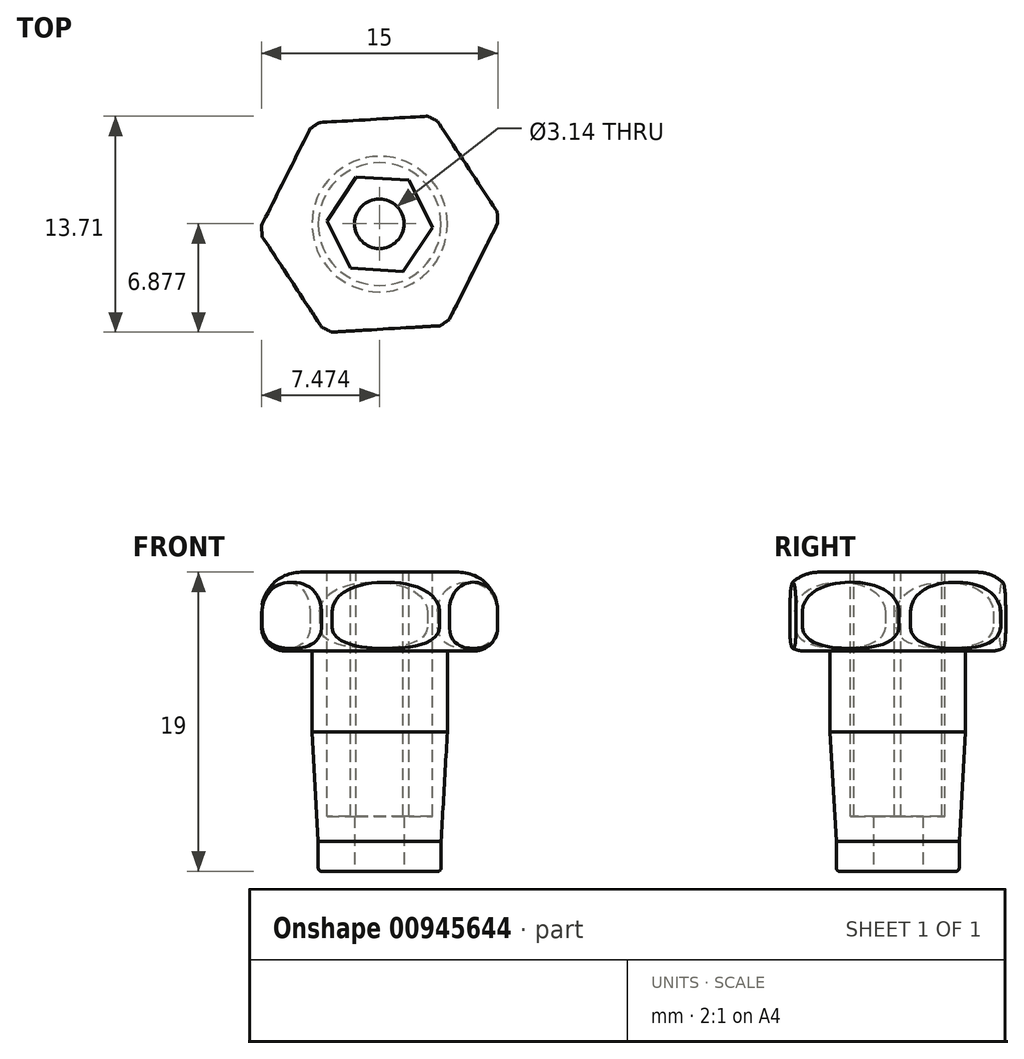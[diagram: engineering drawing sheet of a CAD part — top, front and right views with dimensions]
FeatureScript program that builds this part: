
annotation { "Feature Type Name" : "Feature", "Feature Type Description" : "" }
export const myFeature = defineFeature(function(context is Context, id is Id, definition is map)
    precondition{}
    {
        {
            var Q0;
            Q0=qCreatedBy(makeId("Top.planeOp"),FACE);
            var sketch = newSketch(context, id + "F0", { "sketchPlane" : qUnion([Q0])});
            skCircle(sketch, "E0", {"center": v(-41.47, -26.1) * mm, "radius": 3.9 * mm});
            skSolve(sketch);
        }
        {
            var Q0;
            Q0=qCreatedBy(makeId("Top.planeOp"),FACE);
            var sketch = newSketch(context, id + "F1", { "sketchPlane" : qUnion([Q0])});
            skCircle(sketch, "E1", {"center": v(-41.5, -26.07) * mm, "radius": 1.57 * mm});
            skSolve(sketch);
        }
        {
            var Q0;
            Q0=qSketchRegion(id+"F0",true);
            extrude(context, id + "F2", {"entities" : qUnion([Q0]), "depth" : 14 * mm, "offsetDistance" : 25 * mm});
        }
        {
            var Q0;
            Q0=makeQuery(id+"F2.opExtrude","CAP_FACE",FACE,{"disambiguationData":[OSD([sQuery(id+"F0.wireOp",EDGE,"E0")])],"isStart":false});
            var sketch = newSketch(context, id + "F3", { "sketchPlane" : qUnion([Q0])});
            skCircle(sketch, "E2", {"center": v(-41.47, -26.1) * mm, "radius": 7.5 * mm});
            skSolve(sketch);
        }
        {
            var Q0;
            Q0=qSketchRegion(id+"F3",true);
            extrude(context, id + "F4", {"entities" : qUnion([Q0]), "operationType" : NewBodyOperationType.ADD, "depth" : 5 * mm, "offsetDistance" : 25 * mm});
        }
        {
            var Q0;
            Q0=makeQuery(id+"F4.opExtrude","CAP_FACE",FACE,{"disambiguationData":[OSD([sQuery(id+"F3.wireOp",EDGE,"E2")])],"isStart":false});
            var sketch = newSketch(context, id + "F5", { "sketchPlane" : qUnion([Q0])});
            skCircle(sketch, "E3.cCircle", {"center": v(-41.47, -26.1) * mm, "radius": 2.9 * mm, "construction": true});
            skLineSegment(sketch, "E3.0", {"start": v(-38.13, -26.3) * mm, "end": v(-39.98, -29.1) * mm});
            skLineSegment(sketch, "E3.1", {"start": v(-39.98, -29.1) * mm, "end": v(-43.32, -28.89) * mm});
            skLineSegment(sketch, "E3.2", {"start": v(-43.32, -28.89) * mm, "end": v(-44.81, -25.89) * mm});
            skLineSegment(sketch, "E3.3", {"start": v(-44.81, -25.89) * mm, "end": v(-42.97, -23.1) * mm});
            skLineSegment(sketch, "E3.4", {"start": v(-42.97, -23.1) * mm, "end": v(-39.62, -23.3) * mm});
            skLineSegment(sketch, "E3.5", {"start": v(-39.62, -23.3) * mm, "end": v(-38.13, -26.3) * mm});
            skPoint(sketch, "E3.0.midPoint", {"position": v(-39.05, -27.7) * mm});
            skSolve(sketch);
        }
        {
            var Q0;
            {var subQ0=sQuery(id+"F3.wireOp",EDGE,"E2");Q0=makeQuery(id+"F4.boolean.opBoolean","SPLIT",FACE,{"disambiguationData":[TD([makeQuery(id+"F2.opExtrude","SWEPT_FACE",FACE,{"disambiguationData":[OSD([sQuery(id+"F0.wireOp",EDGE,"E0")])]})])],"derivedFrom":makeQuery(id+"F4.opExtrude","CAP_FACE",FACE,{"disambiguationData":[OSD([subQ0])],"isStart":true})});}
            var sketch = newSketch(context, id + "F6", { "sketchPlane" : qUnion([Q0])});
            skCircle(sketch, "E4", {"center": v(-41.47, 26.1) * mm, "radius": 4.3 * mm});
            skSolve(sketch);
        }
        {
            var Q0;
            Q0=qSketchRegion(id+"F6",true);
            extrude(context, id + "F7", {"entities" : qUnion([Q0]), "operationType" : NewBodyOperationType.ADD, "depth" : 4.1 * mm, "offsetDistance" : 25 * mm});
        }
        {
            var Q0;
            Q0=qSketchRegion(id+"F1",true);
            extrude(context, id + "F8", {"entities" : qUnion([Q0]), "operationType" : NewBodyOperationType.REMOVE, "depth" : 23.4 * mm, "offsetDistance" : 25 * mm});
        }
        {
            var Q0;
            Q0=qSketchRegion(id+"F5",true);
            extrude(context, id + "F9", {"entities" : qUnion([Q0]), "operationType" : NewBodyOperationType.REMOVE, "oppositeDirection" : true, "depth" : 15.5 * mm, "offsetDistance" : 25 * mm});
        }
        {
            var Q0;
            Q0=makeQuery(id+"F2.opExtrude","CAP_EDGE",EDGE,{"disambiguationData":[OSD([sQuery(id+"F0.wireOp",EDGE,"E0")])],"isStart":true});
            fillet(context, id + "F10", {"entities" : qUnion([Q0]), "radius" : 0.2 * mm, "tangentPropagation" : true, "allowEdgeOverflow" : false});
        }
        {
            var Q0;
            Q0=makeQuery(id+"F7.boolean.opBoolean","INTERSECT",EDGE,{"derivedFrom":[makeQuery(id+"F2.opExtrude","SWEPT_FACE",FACE,{"disambiguationData":[OSD([sQuery(id+"F0.wireOp",EDGE,"E0")])]}),makeQuery(id+"F7.opExtrude","CAP_FACE",FACE,{"disambiguationData":[OSD([sQuery(id+"F6.wireOp",EDGE,"E4")])],"isStart":false})]});
            chamfer(context, id + "F11", {"entities" : qUnion([Q0]), "chamferType" : ChamferType.OFFSET_ANGLE, "width" : 8 * mm, "oppositeDirection" : false, "angle" : 3.3 * degree, "tangentPropagation" : true});
        }
        {
            var Q0;
            Q0=makeQuery(id+"F4.opExtrude","CAP_EDGE",EDGE,{"disambiguationData":[OSD([sQuery(id+"F3.wireOp",EDGE,"E2")])],"isStart":true});
            fillet(context, id + "F12", {"entities" : qUnion([Q0]), "radius" : 1.5 * mm, "tangentPropagation" : true, "allowEdgeOverflow" : false});
        }
        {
            var Q0;
            Q0=makeQuery(id+"F4.opExtrude","CAP_EDGE",EDGE,{"disambiguationData":[OSD([sQuery(id+"F3.wireOp",EDGE,"E2")])],"isStart":false});
            fillet(context, id + "F13", {"entities" : qUnion([Q0]), "radius" : 2.5 * mm, "tangentPropagation" : true, "allowEdgeOverflow" : false});
        }
        {
            var Q0;
            Q0=qCreatedBy(makeId("Top.planeOp"),FACE);
            var sketch = newSketch(context, id + "F14", { "sketchPlane" : qUnion([Q0])});
            skPoint(sketch, "E5", {"position": v(-41.47, -26.1) * mm});
            skSolve(sketch);
        }
        {
            var Q0;
            Q0=makeQuery(id+"F4.opExtrude","CAP_FACE",FACE,{"disambiguationData":[OSD([sQuery(id+"F3.wireOp",EDGE,"E2")])],"isStart":false});
            var sketch = newSketch(context, id + "F15", { "sketchPlane" : qUnion([Q0])});
            skCircle(sketch, "E6.cCircle", {"center": v(-41.47, -26.1) * mm, "radius": 6.67 * mm, "construction": true});
            skLineSegment(sketch, "E6.0", {"start": v(-45.7, -19.66) * mm, "end": v(-38.02, -19.21) * mm});
            skLineSegment(sketch, "E6.1", {"start": v(-38.02, -19.21) * mm, "end": v(-33.78, -25.65) * mm});
            skLineSegment(sketch, "E6.2", {"start": v(-33.78, -25.65) * mm, "end": v(-37.24, -32.53) * mm});
            skLineSegment(sketch, "E6.3", {"start": v(-37.24, -32.53) * mm, "end": v(-44.93, -32.98) * mm});
            skLineSegment(sketch, "E6.4", {"start": v(-44.93, -32.98) * mm, "end": v(-49.16, -26.54) * mm});
            skLineSegment(sketch, "E6.5", {"start": v(-49.16, -26.54) * mm, "end": v(-45.7, -19.66) * mm});
            skPoint(sketch, "E6.0.midPoint", {"position": v(-41.86, -19.44) * mm});
            skCircle(sketch, "E7", {"center": v(-41.47, -26.1) * mm, "radius": 8.6 * mm});
            skSolve(sketch);
        }
        {
            var Q0;
            Q0=makeQuery(id+"F15.imprint","IMPRINT",FACE,{"disambiguationData":[TD([[makeQuery(id+"F15.imprint","IMPRINT",EDGE,{"derivedFrom":sQuery(id+"F15.wireOp",EDGE,"E6.0")}),1.0]])]});
            extrude(context, id + "F16", {"entities" : qUnion([Q0]), "operationType" : NewBodyOperationType.REMOVE, "oppositeDirection" : true, "depth" : 6 * mm, "offsetDistance" : 25 * mm});
        }
    });
